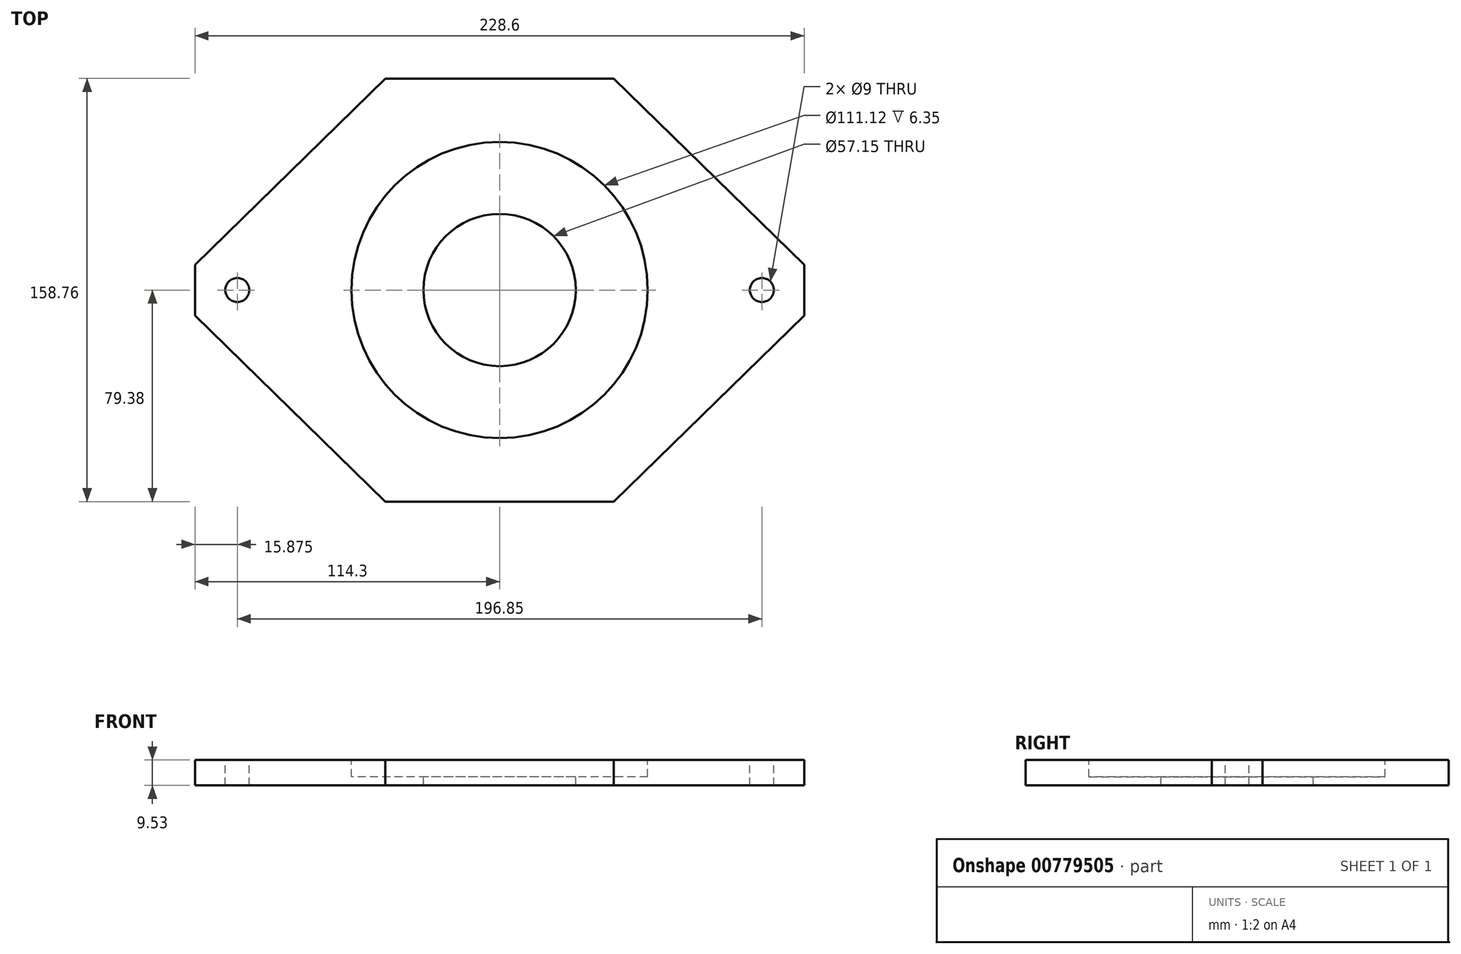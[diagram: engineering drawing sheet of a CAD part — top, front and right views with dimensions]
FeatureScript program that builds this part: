
annotation { "Feature Type Name" : "Feature", "Feature Type Description" : "" }
export const myFeature = defineFeature(function(context is Context, id is Id, definition is map)
    precondition{}
    {
        {
            var Q0;
            Q0=qCreatedBy(makeId("Top.planeOp"),FACE);
            var sketch = newSketch(context, id + "F0", { "sketchPlane" : qUnion([Q0])});
            skLineSegment(sketch, "E0.bottom", {"start": v(114.3, -79.38) * mm, "end": v(-114.3, -79.38) * mm, "construction": true});
            skLineSegment(sketch, "E0.top", {"start": v(114.3, 79.38) * mm, "end": v(-114.3, 79.37) * mm, "construction": true});
            skLineSegment(sketch, "E0.left", {"start": v(114.3, -79.38) * mm, "end": v(114.3, 79.38) * mm, "construction": true});
            skLineSegment(sketch, "E0.right", {"start": v(-114.3, -79.38) * mm, "end": v(-114.3, 79.37) * mm, "construction": true});
            skPoint(sketch, "E0.middle", {"position": v(0, 0) * mm});
            skLineSegment(sketch, "E1", {"start": v(142.63, 0) * mm, "end": v(-177.9, 0) * mm, "construction": true});
            skLineSegment(sketch, "E2", {"start": v(-114.3, 9.52) * mm, "end": v(-114.3, -9.53) * mm});
            skLineSegment(sketch, "E3.MirrorCS", {"start": v(114.3, 9.52) * mm, "end": v(114.3, -9.53) * mm});
            skLineSegment(sketch, "E4", {"start": v(0, 106) * mm, "end": v(0, -127.84) * mm, "construction": true});
            skPoint(sketch, "E4.endSnap0", {"position": v(0, -79.38) * mm});
            skLineSegment(sketch, "E5", {"start": v(-42.86, 79.38) * mm, "end": v(42.86, 79.38) * mm});
            skLineSegment(sketch, "E6.MirrorCS", {"start": v(-42.86, -79.38) * mm, "end": v(42.86, -79.38) * mm});
            skLineSegment(sketch, "E7", {"start": v(-114.3, -9.53) * mm, "end": v(-42.86, -79.38) * mm});
            skLineSegment(sketch, "E8", {"start": v(42.86, -79.38) * mm, "end": v(114.3, -9.53) * mm});
            skLineSegment(sketch, "E9", {"start": v(114.3, 9.52) * mm, "end": v(42.86, 79.38) * mm});
            skLineSegment(sketch, "E10", {"start": v(-42.86, 79.38) * mm, "end": v(-114.3, 9.52) * mm});
            skSolve(sketch);
        }
        {
            var Q0;
            Q0=makeQuery(id+"F0.imprint","IMPRINT",FACE,{"disambiguationData":[TD([[makeQuery(id+"F0.imprint","IMPRINT",EDGE,{"derivedFrom":sQuery(id+"F0.wireOp",EDGE,"E2")}),1.0]])]});
            extrude(context, id + "F1", {"entities" : qUnion([Q0]), "depth" : 9.52 * mm, "offsetDistance" : 25.4 * mm});
        }
        {
            var Q0;
            Q0=makeQuery(id+"F1.opExtrude","CAP_FACE",FACE,{"disambiguationData":[OSD([sQuery(id+"F0.wireOp",EDGE,"E2"),sQuery(id+"F0.wireOp",EDGE,"E3.MirrorCS"),sQuery(id+"F0.wireOp",EDGE,"E5"),sQuery(id+"F0.wireOp",EDGE,"E6.MirrorCS"),sQuery(id+"F0.wireOp",EDGE,"E7"),sQuery(id+"F0.wireOp",EDGE,"E8"),sQuery(id+"F0.wireOp",EDGE,"E9"),sQuery(id+"F0.wireOp",EDGE,"E10")])],"isStart":false});
            var sketch = newSketch(context, id + "F2", { "sketchPlane" : qUnion([Q0])});
            skCircle(sketch, "E11", {"center": v(0, 0) * mm, "radius": 55.56 * mm});
            skSolve(sketch);
        }
        {
            var Q0;
            Q0=makeQuery(id+"F2.imprint","IMPRINT",FACE,{"disambiguationData":[TD([[makeQuery(id+"F2.imprint","IMPRINT",EDGE,{"derivedFrom":sQuery(id+"F2.wireOp",EDGE,"E11")}),1.0]])]});
            extrude(context, id + "F3", {"entities" : qUnion([Q0]), "operationType" : NewBodyOperationType.REMOVE, "oppositeDirection" : true, "depth" : 6.35 * mm, "offsetDistance" : 25.4 * mm});
        }
        {
            var Q0;
            Q0=makeQuery(id+"F1.opExtrude","CAP_FACE",FACE,{"disambiguationData":[OSD([sQuery(id+"F0.wireOp",EDGE,"E2"),sQuery(id+"F0.wireOp",EDGE,"E3.MirrorCS"),sQuery(id+"F0.wireOp",EDGE,"E5"),sQuery(id+"F0.wireOp",EDGE,"E6.MirrorCS"),sQuery(id+"F0.wireOp",EDGE,"E7"),sQuery(id+"F0.wireOp",EDGE,"E8"),sQuery(id+"F0.wireOp",EDGE,"E9"),sQuery(id+"F0.wireOp",EDGE,"E10")])],"isStart":false});
            var sketch = newSketch(context, id + "F4", { "sketchPlane" : qUnion([Q0])});
            skPoint(sketch, "E12", {"position": v(-98.43, 0) * mm});
            skPoint(sketch, "E13.MirrorP", {"position": v(98.43, 0) * mm});
            skSolve(sketch);
        }
        {
            var Q0;
            Q0=sQuery(id+"F4.wireOp",VERTEX,"E12");
            var Q1;
            Q1=sQuery(id+"F4.wireOp",VERTEX,"E13.MirrorP");
            var Q2;
            Q2=makeQuery(id+"F1.opExtrude","SWEPT_BODY",BODY,{"disambiguationData":[OSD([sQuery(id+"F0.wireOp",EDGE,"E2"),sQuery(id+"F0.wireOp",EDGE,"E3.MirrorCS"),sQuery(id+"F0.wireOp",EDGE,"E5"),sQuery(id+"F0.wireOp",EDGE,"E6.MirrorCS"),sQuery(id+"F0.wireOp",EDGE,"E7"),sQuery(id+"F0.wireOp",EDGE,"E8"),sQuery(id+"F0.wireOp",EDGE,"E9"),sQuery(id+"F0.wireOp",EDGE,"E10")])]});
            hole(context, id + "F5", {"style" : HoleStyle.SIMPLE, "endStyle" : HoleEndStyle.THROUGH, "standardTappedOrClearance" : lookupTablePath({ "standard" : "ISO", "engagement" : "50%", "pitch" : "1.5 mm", "size" : "M10", "type" : "Tapped" }), "standardBlindInLast" : lookupTablePath({ "standard" : "ISO", "engagement" : "50%", "pitch" : "1.5 mm", "size" : "M10", "type" : "Tapped" }), "holeDiameter" : 9 * mm, "majorDiameter" : 10 * mm, "showTappedDepth" : true, "isTappedThrough" : true, "tappedDepth" : 3.63 * mm, "tapClearance" : 3, "startFromSketch" : true, "locations" : qUnion([Q0, Q1]), "scope" : qUnion([Q2])});
        }
        {
            var Q0;
            Q0=makeQuery(id+"F3.boolean.opBoolean","COPY",FACE,{"derivedFrom":makeQuery(id+"F3.opExtrude","CAP_FACE",FACE,{"disambiguationData":[OSD([sQuery(id+"F2.wireOp",EDGE,"E11")])],"isStart":false})});
            var sketch = newSketch(context, id + "F6", { "sketchPlane" : qUnion([Q0])});
            skCircle(sketch, "E14", {"center": v(0, 0) * mm, "radius": 28.58 * mm});
            skSolve(sketch);
        }
        {
            var Q0;
            Q0=makeQuery(id+"F6.imprint","IMPRINT",FACE,{"disambiguationData":[TD([[makeQuery(id+"F6.imprint","IMPRINT",EDGE,{"derivedFrom":sQuery(id+"F6.wireOp",EDGE,"E14")}),1.0]])]});
            extrude(context, id + "F7", {"entities" : qUnion([Q0]), "operationType" : NewBodyOperationType.REMOVE, "endBound" : BoundingType.THROUGH_ALL, "oppositeDirection" : true, "depth" : 25.4 * mm, "offsetDistance" : 25.4 * mm});
        }
    });
